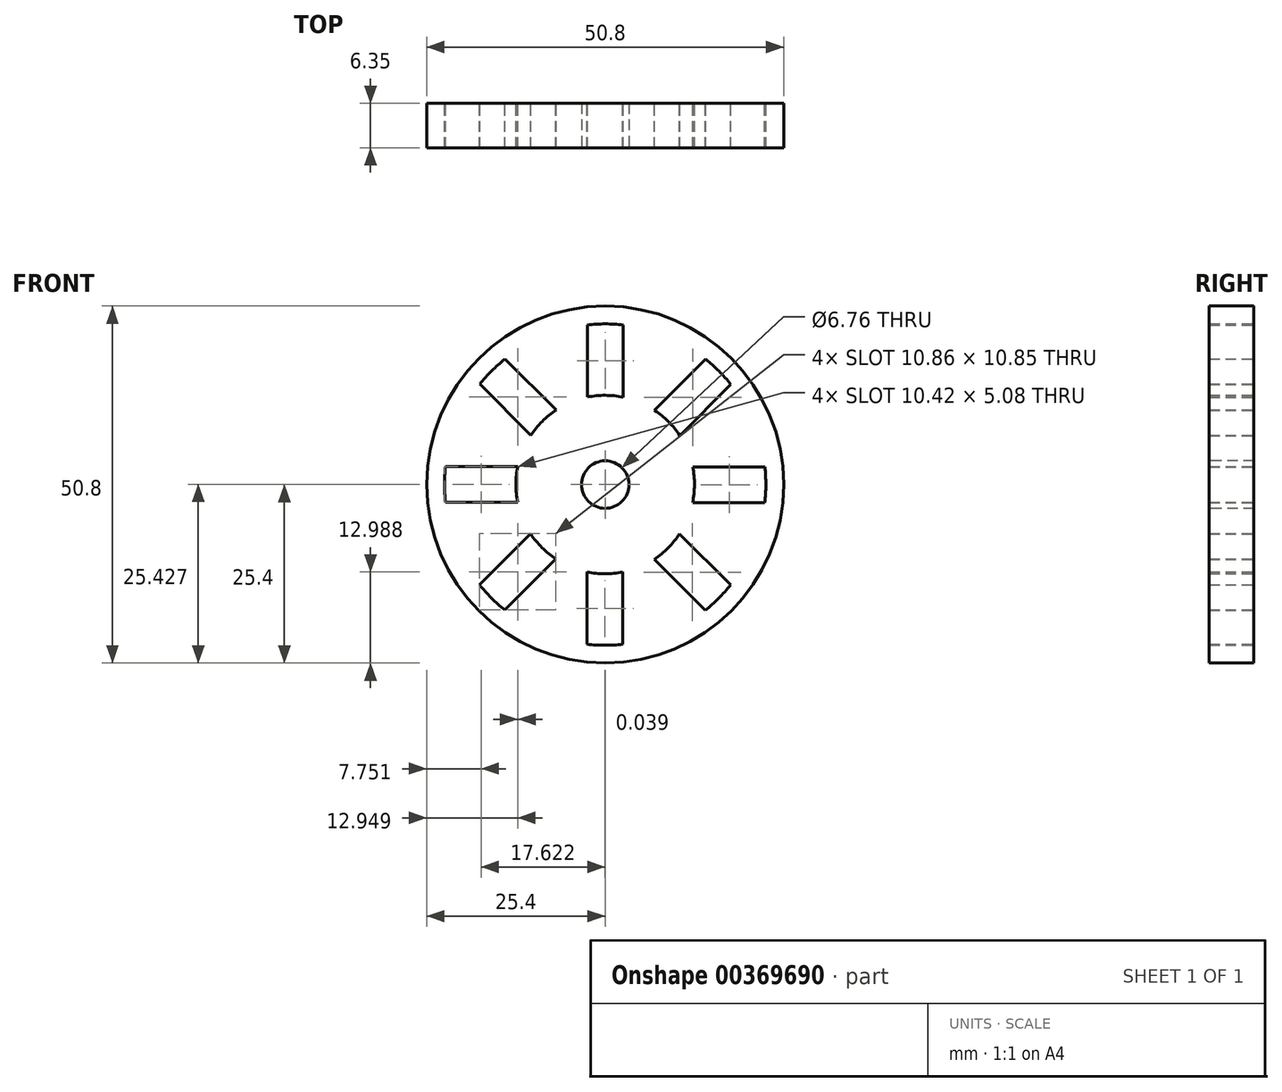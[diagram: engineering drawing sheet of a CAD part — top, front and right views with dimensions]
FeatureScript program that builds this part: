
annotation { "Feature Type Name" : "Feature", "Feature Type Description" : "" }
export const myFeature = defineFeature(function(context is Context, id is Id, definition is map)
    precondition{}
    {
        {
            var Q0;
            Q0=qCreatedBy(makeId("Front.planeOp"),FACE);
            var sketch = newSketch(context, id + "F0", { "sketchPlane" : qUnion([Q0])});
            skCircle(sketch, "E0", {"center": v(0, 0) * mm, "radius": 25.4 * mm});
            skArc(sketch, "E1", {"start": v(-14.25, 17.88) * mm, "mid": v(-16.15, 16.18) * mm, "end": v(-17.84, 14.29) * mm});
            skArc(sketch, "E2", {"start": v(-6.98, 10.6) * mm, "mid": v(-8.96, 9) * mm, "end": v(-10.58, 7.03) * mm});
            skLineSegment(sketch, "E3", {"start": v(-2.51, 22.72) * mm, "end": v(-2.51, 12.45) * mm});
            skLineSegment(sketch, "E4", {"start": v(2.57, 22.72) * mm, "end": v(2.57, 12.44) * mm});
            skLineSegment(sketch, "E5", {"start": v(2.57, 22.72) * mm, "end": v(-2.51, 22.72) * mm, "construction": true});
            skLineSegment(sketch, "E6.1.0", {"start": v(-14.25, 17.88) * mm, "end": v(-6.98, 10.6) * mm});
            skLineSegment(sketch, "E6.1.1", {"start": v(-17.84, 14.29) * mm, "end": v(-10.58, 7.03) * mm});
            skLineSegment(sketch, "E6.2.0", {"start": v(-22.72, 2.57) * mm, "end": v(-12.44, 2.57) * mm});
            skLineSegment(sketch, "E6.2.1", {"start": v(-22.72, -2.51) * mm, "end": v(-12.45, -2.51) * mm});
            skLineSegment(sketch, "E6.3.0", {"start": v(-17.88, -14.25) * mm, "end": v(-10.6, -6.98) * mm});
            skLineSegment(sketch, "E6.3.1", {"start": v(-14.29, -17.84) * mm, "end": v(-7.03, -10.58) * mm});
            skLineSegment(sketch, "E6.4.0", {"start": v(-2.57, -22.72) * mm, "end": v(-2.57, -12.44) * mm});
            skLineSegment(sketch, "E6.4.1", {"start": v(2.51, -22.72) * mm, "end": v(2.51, -12.45) * mm});
            skLineSegment(sketch, "E6.5.0", {"start": v(14.25, -17.88) * mm, "end": v(6.98, -10.6) * mm});
            skLineSegment(sketch, "E6.5.1", {"start": v(17.84, -14.29) * mm, "end": v(10.58, -7.03) * mm});
            skLineSegment(sketch, "E6.6.0", {"start": v(22.72, -2.57) * mm, "end": v(12.44, -2.57) * mm});
            skLineSegment(sketch, "E6.6.1", {"start": v(22.72, 2.51) * mm, "end": v(12.45, 2.51) * mm});
            skLineSegment(sketch, "E6.7.0", {"start": v(17.88, 14.25) * mm, "end": v(10.6, 6.98) * mm});
            skLineSegment(sketch, "E6.7.1", {"start": v(14.29, 17.84) * mm, "end": v(7.03, 10.58) * mm});
            skArc(sketch, "E7.trimOffspring", {"start": v(2.57, 12.44) * mm, "mid": v(0.03, 12.7) * mm, "end": v(-2.51, 12.45) * mm});
            skArc(sketch, "E8.trimOffspring", {"start": v(2.57, 22.72) * mm, "mid": v(0.03, 22.86) * mm, "end": v(-2.51, 22.72) * mm});
            skArc(sketch, "E9.trimOffspring", {"start": v(17.88, 14.25) * mm, "mid": v(16.18, 16.15) * mm, "end": v(14.29, 17.84) * mm});
            skArc(sketch, "E10.trimOffspring", {"start": v(10.6, 6.98) * mm, "mid": v(9, 8.96) * mm, "end": v(7.03, 10.58) * mm});
            skArc(sketch, "E11.trimOffspring", {"start": v(12.44, -2.57) * mm, "mid": v(12.7, -0.03) * mm, "end": v(12.45, 2.51) * mm});
            skArc(sketch, "E12.trimOffspring", {"start": v(22.72, -2.57) * mm, "mid": v(22.86, -0.03) * mm, "end": v(22.72, 2.51) * mm});
            skArc(sketch, "E13.trimOffspring", {"start": v(14.25, -17.88) * mm, "mid": v(16.15, -16.18) * mm, "end": v(17.84, -14.29) * mm});
            skArc(sketch, "E14.trimOffspring", {"start": v(6.98, -10.6) * mm, "mid": v(8.96, -9) * mm, "end": v(10.58, -7.03) * mm});
            skArc(sketch, "E15.trimOffspring", {"start": v(-2.57, -12.44) * mm, "mid": v(-0.03, -12.7) * mm, "end": v(2.51, -12.45) * mm});
            skArc(sketch, "E16.trimOffspring", {"start": v(-2.57, -22.72) * mm, "mid": v(-0.03, -22.86) * mm, "end": v(2.51, -22.72) * mm});
            skArc(sketch, "E17.trimOffspring", {"start": v(-10.6, -6.98) * mm, "mid": v(-9, -8.96) * mm, "end": v(-7.03, -10.58) * mm});
            skArc(sketch, "E18.trimOffspring", {"start": v(-17.88, -14.25) * mm, "mid": v(-16.18, -16.15) * mm, "end": v(-14.29, -17.84) * mm});
            skArc(sketch, "E19.trimOffspring", {"start": v(-12.44, 2.57) * mm, "mid": v(-12.7, 0.03) * mm, "end": v(-12.45, -2.51) * mm});
            skArc(sketch, "E20.trimOffspring", {"start": v(-22.72, 2.57) * mm, "mid": v(-22.86, 0.03) * mm, "end": v(-22.72, -2.51) * mm});
            skSolve(sketch);
        }
        {
            var Q0;
            Q0=makeQuery(id+"F0.imprint","IMPRINT",FACE,{"disambiguationData":[TD([[makeQuery(id+"F0.imprint","IMPRINT",EDGE,{"derivedFrom":sQuery(id+"F0.wireOp",EDGE,"E0")}),1.0]])]});
            extrude(context, id + "F1", {"entities" : qUnion([Q0]), "depth" : 6.35 * mm, "offsetDistance" : 25.4 * mm});
        }
        {
            var Q0;
            Q0=makeQuery(id+"F1.opExtrude","CAP_FACE",FACE,{"disambiguationData":[OSD([sQuery(id+"F0.wireOp",EDGE,"E0"),sQuery(id+"F0.wireOp",EDGE,"E1"),sQuery(id+"F0.wireOp",EDGE,"E2"),sQuery(id+"F0.wireOp",EDGE,"E3"),sQuery(id+"F0.wireOp",EDGE,"E4"),sQuery(id+"F0.wireOp",EDGE,"E6.1.0"),sQuery(id+"F0.wireOp",EDGE,"E6.1.1"),sQuery(id+"F0.wireOp",EDGE,"E6.2.0"),sQuery(id+"F0.wireOp",EDGE,"E6.2.1"),sQuery(id+"F0.wireOp",EDGE,"E6.3.0"),sQuery(id+"F0.wireOp",EDGE,"E6.3.1"),sQuery(id+"F0.wireOp",EDGE,"E6.4.0"),sQuery(id+"F0.wireOp",EDGE,"E6.4.1"),sQuery(id+"F0.wireOp",EDGE,"E6.5.0"),sQuery(id+"F0.wireOp",EDGE,"E6.5.1"),sQuery(id+"F0.wireOp",EDGE,"E6.6.0"),sQuery(id+"F0.wireOp",EDGE,"E6.6.1"),sQuery(id+"F0.wireOp",EDGE,"E6.7.0"),sQuery(id+"F0.wireOp",EDGE,"E6.7.1"),sQuery(id+"F0.wireOp",EDGE,"E7.trimOffspring"),sQuery(id+"F0.wireOp",EDGE,"E8.trimOffspring"),sQuery(id+"F0.wireOp",EDGE,"E9.trimOffspring"),sQuery(id+"F0.wireOp",EDGE,"E10.trimOffspring"),sQuery(id+"F0.wireOp",EDGE,"E11.trimOffspring"),sQuery(id+"F0.wireOp",EDGE,"E12.trimOffspring"),sQuery(id+"F0.wireOp",EDGE,"E13.trimOffspring"),sQuery(id+"F0.wireOp",EDGE,"E14.trimOffspring"),sQuery(id+"F0.wireOp",EDGE,"E15.trimOffspring"),sQuery(id+"F0.wireOp",EDGE,"E16.trimOffspring"),sQuery(id+"F0.wireOp",EDGE,"E17.trimOffspring"),sQuery(id+"F0.wireOp",EDGE,"E18.trimOffspring"),sQuery(id+"F0.wireOp",EDGE,"E19.trimOffspring"),sQuery(id+"F0.wireOp",EDGE,"E20.trimOffspring")])],"isStart":false});
            var sketch = newSketch(context, id + "F2", { "sketchPlane" : qUnion([Q0])});
            skPoint(sketch, "E21", {"position": v(0, 0) * mm});
            skSolve(sketch);
        }
        {
            var Q0;
            Q0=sQuery(id+"F2.wireOp",VERTEX,"E21");
            var Q1;
            Q1=makeQuery(id+"F1.opExtrude","SWEPT_BODY",BODY,{"disambiguationData":[OSD([sQuery(id+"F0.wireOp",EDGE,"E0"),sQuery(id+"F0.wireOp",EDGE,"E1"),sQuery(id+"F0.wireOp",EDGE,"E2"),sQuery(id+"F0.wireOp",EDGE,"E3"),sQuery(id+"F0.wireOp",EDGE,"E4"),sQuery(id+"F0.wireOp",EDGE,"E6.1.0"),sQuery(id+"F0.wireOp",EDGE,"E6.1.1"),sQuery(id+"F0.wireOp",EDGE,"E6.2.0"),sQuery(id+"F0.wireOp",EDGE,"E6.2.1"),sQuery(id+"F0.wireOp",EDGE,"E6.3.0"),sQuery(id+"F0.wireOp",EDGE,"E6.3.1"),sQuery(id+"F0.wireOp",EDGE,"E6.4.0"),sQuery(id+"F0.wireOp",EDGE,"E6.4.1"),sQuery(id+"F0.wireOp",EDGE,"E6.5.0"),sQuery(id+"F0.wireOp",EDGE,"E6.5.1"),sQuery(id+"F0.wireOp",EDGE,"E6.6.0"),sQuery(id+"F0.wireOp",EDGE,"E6.6.1"),sQuery(id+"F0.wireOp",EDGE,"E6.7.0"),sQuery(id+"F0.wireOp",EDGE,"E6.7.1"),sQuery(id+"F0.wireOp",EDGE,"E7.trimOffspring"),sQuery(id+"F0.wireOp",EDGE,"E8.trimOffspring"),sQuery(id+"F0.wireOp",EDGE,"E9.trimOffspring"),sQuery(id+"F0.wireOp",EDGE,"E10.trimOffspring"),sQuery(id+"F0.wireOp",EDGE,"E11.trimOffspring"),sQuery(id+"F0.wireOp",EDGE,"E12.trimOffspring"),sQuery(id+"F0.wireOp",EDGE,"E13.trimOffspring"),sQuery(id+"F0.wireOp",EDGE,"E14.trimOffspring"),sQuery(id+"F0.wireOp",EDGE,"E15.trimOffspring"),sQuery(id+"F0.wireOp",EDGE,"E16.trimOffspring"),sQuery(id+"F0.wireOp",EDGE,"E17.trimOffspring"),sQuery(id+"F0.wireOp",EDGE,"E18.trimOffspring"),sQuery(id+"F0.wireOp",EDGE,"E19.trimOffspring"),sQuery(id+"F0.wireOp",EDGE,"E20.trimOffspring")])]});
            hole(context, id + "F3", {"style" : HoleStyle.SIMPLE, "endStyle" : HoleEndStyle.BLIND, "standardTappedOrClearance" : lookupTablePath({ "standard" : "ANSI", "fit" : "Normal (ASME)", "size" : "1/4", "type" : "Clearance" }), "standardBlindInLast" : lookupTablePath({ "fit" : "Free", "standard" : "ANSI", "size" : "1/4", "type" : "Clearance" }), "holeDiameter" : 6.76 * mm, "majorDiameter" : 6.35 * mm, "holeDepth" : 11.9 * mm, "tappedDepth" : 9.53 * mm, "tapClearance" : 3, "startFromSketch" : true, "locations" : qUnion([Q0]), "scope" : qUnion([Q1])});
        }
    });
